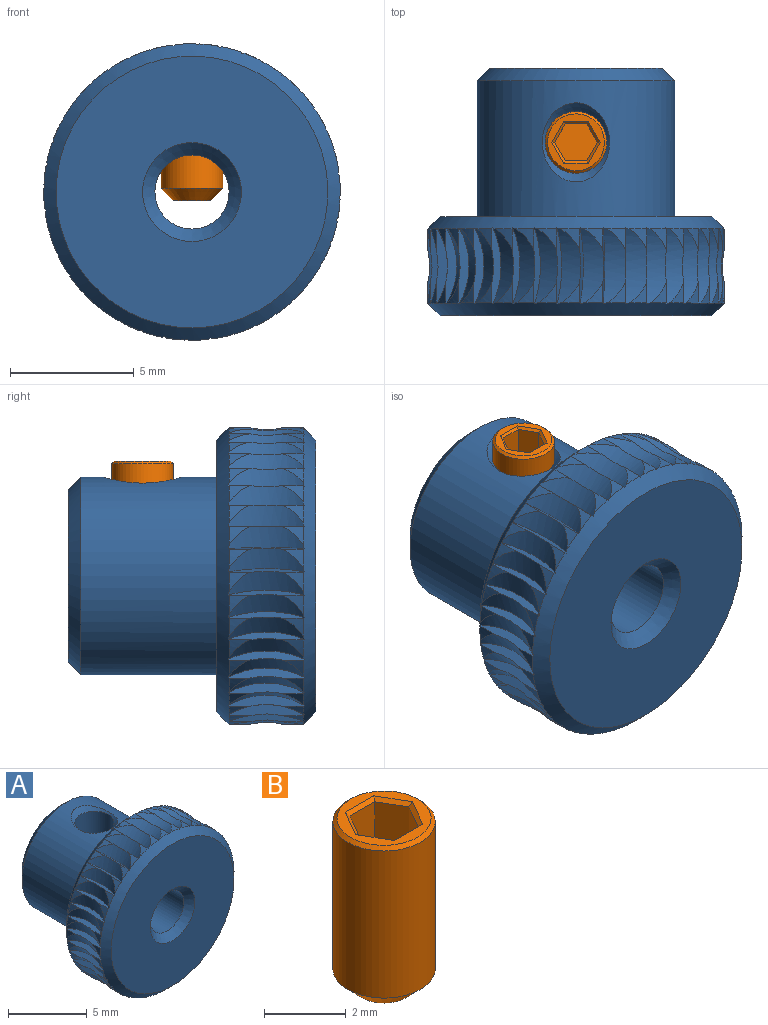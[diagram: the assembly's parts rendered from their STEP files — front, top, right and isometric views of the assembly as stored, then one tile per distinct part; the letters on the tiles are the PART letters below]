
ASSEMBLY  parts=2 mates=1
PART A: 172 faces, bbox 12.6x10x12.6 mm
  f0: cylinder r=1.5mm len=9mm, axis (0,-1,0), area 79.3mm2, adj f167,f168,f170
  f1: cylinder r=4mm len=8mm, axis (0,1,0), area 131.3mm2, adj f164,f165,f171
  f2: cylinder r=6mm len=0.84mm, axis (0,-1,0), area 0.3mm2, adj f129,f130,f169
  f3: cylinder r=6mm len=0.84mm, axis (0,-1,0), area 0.3mm2, adj f127,f128,f169
  f4: cylinder r=6mm len=0.84mm, axis (0,-1,0), area 0.3mm2, adj f125,f126,f169
  f5: cylinder r=6mm len=0.84mm, axis (0,-1,0), area 0.3mm2, adj f119,f124,f169
  f6: cylinder r=6mm len=0.84mm, axis (0,-1,0), area 0.3mm2, adj f122,f123,f169
  f7: cylinder r=6mm len=0.84mm, axis (0,-1,0), area 0.3mm2, adj f120,f121,f169
  f8: cylinder r=6mm len=0.84mm, axis (0,-1,0), area 0.3mm2, adj f116,f117,f169
  f9: cylinder r=6mm len=0.84mm, axis (0,-1,0), area 0.3mm2, adj f86,f115,f169
  f10: cylinder r=6mm len=0.84mm, axis (0,-1,0), area 0.3mm2, adj f113,f114,f169
  f11: cylinder r=6mm len=0.84mm, axis (0,-1,0), area 0.3mm2, adj f111,f112,f169
  f12: cylinder r=6mm len=0.84mm, axis (0,-1,0), area 0.3mm2, adj f109,f110,f169
  f13: cylinder r=6mm len=0.84mm, axis (0,-1,0), area 0.3mm2, adj f103,f108,f169
  f14: cylinder r=6mm len=0.84mm, axis (0,-1,0), area 0.3mm2, adj f106,f107,f169
  f15: cylinder r=6mm len=0.84mm, axis (0,-1,0), area 0.3mm2, adj f104,f105,f169
  f16: cylinder r=6mm len=0.84mm, axis (0,-1,0), area 0.3mm2, adj f101,f102,f169
  f17: cylinder r=6mm len=0.84mm, axis (0,-1,0), area 0.3mm2, adj f87,f100,f169
  f18: cylinder r=6mm len=0.84mm, axis (0,-1,0), area 0.3mm2, adj f98,f99,f169
  f19: cylinder r=6mm len=0.84mm, axis (0,-1,0), area 0.3mm2, adj f96,f97,f169
  f20: cylinder r=6mm len=0.84mm, axis (0,-1,0), area 0.3mm2, adj f94,f95,f169
  f21: cylinder r=6mm len=0.84mm, axis (0,-1,0), area 0.3mm2, adj f88,f93,f169
  f22: cylinder r=6mm len=0.84mm, axis (0,-1,0), area 0.3mm2, adj f91,f92,f169
  f23: cylinder r=6mm len=0.84mm, axis (0,-1,0), area 0.3mm2, adj f89,f90,f169
  f24: cylinder r=6mm len=0.84mm, axis (0,-1,0), area 0.3mm2, adj f84,f162,f169
  f25: cylinder r=6mm len=0.84mm, axis (0,-1,0), area 0.3mm2, adj f160,f161,f169
  f26: cylinder r=6mm len=0.84mm, axis (0,-1,0), area 0.3mm2, adj f83,f159,f169
  f27: cylinder r=6mm len=0.84mm, axis (0,-1,0), area 0.3mm2, adj f157,f158,f169
  f28: cylinder r=6mm len=0.84mm, axis (0,-1,0), area 0.3mm2, adj f155,f156,f169
  f29: cylinder r=6mm len=0.84mm, axis (0,-1,0), area 0.3mm2, adj f149,f154,f169
  f30: cylinder r=6mm len=0.84mm, axis (0,-1,0), area 0.3mm2, adj f152,f153,f169
  f31: cylinder r=6mm len=0.84mm, axis (0,-1,0), area 0.3mm2, adj f150,f151,f169
  f32: cylinder r=6mm len=0.84mm, axis (0,-1,0), area 0.3mm2, adj f147,f148,f169
  f33: cylinder r=6mm len=0.84mm, axis (0,-1,0), area 0.3mm2, adj f85,f146,f169
  f34: cylinder r=6mm len=0.84mm, axis (0,-1,0), area 0.3mm2, adj f144,f145,f169
  f35: cylinder r=6mm len=0.84mm, axis (0,-1,0), area 0.3mm2, adj f142,f143,f169
  f36: cylinder r=6mm len=0.84mm, axis (0,-1,0), area 0.3mm2, adj f140,f141,f169
  f37: cylinder r=6mm len=0.84mm, axis (0,-1,0), area 0.3mm2, adj f134,f139,f169
  f38: cylinder r=6mm len=0.84mm, axis (0,-1,0), area 0.3mm2, adj f137,f138,f169
  f39: cylinder r=6mm len=0.84mm, axis (0,-1,0), area 0.3mm2, adj f135,f136,f169
  f40: cylinder r=6mm len=0.84mm, axis (0,-1,0), area 0.3mm2, adj f132,f133,f169
  f41: cylinder r=6mm len=0.84mm, axis (0,-1,0), area 0.3mm2, adj f122,f123,f166
  f42: cylinder r=6mm len=0.84mm, axis (0,-1,0), area 0.3mm2, adj f119,f124,f166
  f43: cylinder r=6mm len=0.84mm, axis (0,-1,0), area 0.3mm2, adj f125,f126,f166
  f44: cylinder r=6mm len=0.84mm, axis (0,-1,0), area 0.3mm2, adj f127,f128,f166
  f45: cylinder r=6mm len=0.84mm, axis (0,-1,0), area 0.3mm2, adj f129,f130,f166
  f46: cylinder r=6mm len=0.84mm, axis (0,-1,0), area 0.3mm2, adj f118,f131,f166
  f47: cylinder r=6mm len=0.84mm, axis (0,-1,0), area 0.3mm2, adj f132,f133,f166
  f48: cylinder r=6mm len=0.84mm, axis (0,-1,0), area 0.3mm2, adj f135,f136,f166
  f49: cylinder r=6mm len=0.84mm, axis (0,-1,0), area 0.3mm2, adj f137,f138,f166
  f50: cylinder r=6mm len=0.84mm, axis (0,-1,0), area 0.3mm2, adj f134,f139,f166
  f51: cylinder r=6mm len=0.84mm, axis (0,-1,0), area 0.3mm2, adj f140,f141,f166
  f52: cylinder r=6mm len=0.84mm, axis (0,-1,0), area 0.3mm2, adj f142,f143,f166
  f53: cylinder r=6mm len=0.84mm, axis (0,-1,0), area 0.3mm2, adj f144,f145,f166
  f54: cylinder r=6mm len=0.84mm, axis (0,-1,0), area 0.3mm2, adj f85,f146,f166
  f55: cylinder r=6mm len=0.84mm, axis (0,-1,0), area 0.3mm2, adj f147,f148,f166
  f56: cylinder r=6mm len=0.84mm, axis (0,-1,0), area 0.3mm2, adj f150,f151,f166
  f57: cylinder r=6mm len=0.84mm, axis (0,-1,0), area 0.3mm2, adj f152,f153,f166
  f58: cylinder r=6mm len=0.84mm, axis (0,-1,0), area 0.3mm2, adj f149,f154,f166
  f59: cylinder r=6mm len=0.84mm, axis (0,-1,0), area 0.3mm2, adj f155,f156,f166
  f60: cylinder r=6mm len=0.84mm, axis (0,-1,0), area 0.3mm2, adj f157,f158,f166
  f61: cylinder r=6mm len=0.84mm, axis (0,-1,0), area 0.3mm2, adj f83,f159,f166
  f62: cylinder r=6mm len=0.84mm, axis (0,-1,0), area 0.3mm2, adj f160,f161,f166
  f63: cylinder r=6mm len=0.84mm, axis (0,-1,0), area 0.3mm2, adj f84,f162,f166
  f64: cylinder r=6mm len=0.84mm, axis (0,-1,0), area 0.3mm2, adj f89,f90,f166
  f65: cylinder r=6mm len=0.84mm, axis (0,-1,0), area 0.3mm2, adj f91,f92,f166
  f66: cylinder r=6mm len=0.84mm, axis (0,-1,0), area 0.3mm2, adj f88,f93,f166
  f67: cylinder r=6mm len=0.84mm, axis (0,-1,0), area 0.3mm2, adj f94,f95,f166
  f68: cylinder r=6mm len=0.84mm, axis (0,-1,0), area 0.3mm2, adj f96,f97,f166
  f69: cylinder r=6mm len=0.84mm, axis (0,-1,0), area 0.3mm2, adj f98,f99,f166
  f70: cylinder r=6mm len=0.84mm, axis (0,-1,0), area 0.3mm2, adj f87,f100,f166
  f71: cylinder r=6mm len=0.84mm, axis (0,-1,0), area 0.3mm2, adj f101,f102,f166
  f72: cylinder r=6mm len=0.84mm, axis (0,-1,0), area 0.3mm2, adj f104,f105,f166
  f73: cylinder r=6mm len=0.84mm, axis (0,-1,0), area 0.3mm2, adj f106,f107,f166
  f74: cylinder r=6mm len=0.84mm, axis (0,-1,0), area 0.3mm2, adj f103,f108,f166
  f75: cylinder r=6mm len=0.84mm, axis (0,-1,0), area 0.3mm2, adj f109,f110,f166
  f76: cylinder r=6mm len=0.84mm, axis (0,-1,0), area 0.3mm2, adj f111,f112,f166
  f77: cylinder r=6mm len=0.84mm, axis (0,-1,0), area 0.3mm2, adj f113,f114,f166
  f78: cylinder r=6mm len=0.84mm, axis (0,-1,0), area 0.3mm2, adj f86,f115,f166
  f79: cylinder r=6mm len=0.84mm, axis (0,-1,0), area 0.3mm2, adj f116,f117,f166
  f80: cylinder r=6mm len=0.84mm, axis (0,-1,0), area 0.3mm2, adj f120,f121,f166
  f81: cylinder r=6mm len=0.84mm, axis (0,-1,0), area 0.3mm2, adj f118,f131,f169
  f82: plane 11x11mm, normal (0,-1,0), area 82.5mm2, adj f168,f169
  f83: cylinder r=3mm len=3.07mm, axis (-0.16,0,-0.99), area 2.2mm2, adj f26,f61,f159,f160,f166,f169
  f84: cylinder r=3mm len=3.07mm, axis (0.16,0,-0.99), area 2.2mm2, adj f24,f63,f90,f162,f166,f169
  f85: cylinder r=3mm len=3.07mm, axis (-0.95,0,-0.31), area 2.2mm2, adj f33,f54,f146,f147,f166,f169
  f86: cylinder r=3mm len=3.07mm, axis (0.59,0,0.81), area 2.2mm2, adj f9,f78,f115,f116,f166,f169
  f87: cylinder r=3mm len=3.07mm, axis (0.95,0,-0.31), area 2.2mm2, adj f17,f70,f100,f101,f166,f169
  f88: cylinder r=3mm len=3.07mm, axis (0.59,0,-0.81), area 2.2mm2, adj f21,f66,f93,f94,f166,f169
  f89: cylinder r=3mm len=3.07mm, axis (0.31,0,-0.95), area 2.2mm2, adj f23,f64,f90,f91,f166,f169
  f90: plane 3.09x0.47mm, normal (-0.16,0,0.99), area 0.9mm2, adj f23,f64,f84,f89,f166,f169
  f91: plane 3.09x0.46mm, normal (-0.31,0,0.95), area 0.9mm2, adj f22,f65,f89,f92,f166,f169
  f92: cylinder r=3mm len=3.07mm, axis (0.45,0,-0.89), area 2.2mm2, adj f22,f65,f91,f93,f166,f169
  f93: plane 3.09x0.43mm, normal (-0.45,0,0.89), area 0.9mm2, adj f21,f66,f88,f92,f166,f169
  f94: plane 3.09x0.39mm, normal (-0.59,0,0.81), area 0.9mm2, adj f20,f67,f88,f95,f166,f169
  f95: cylinder r=3mm len=3.07mm, axis (0.71,0,-0.71), area 2.2mm2, adj f20,f67,f94,f97,f166,f169
  f96: cylinder r=3mm len=3.07mm, axis (0.81,0,-0.59), area 2.2mm2, adj f19,f68,f97,f98,f166,f169
  f97: plane 3.09x0.35mm, normal (-0.71,0,0.71), area 0.9mm2, adj f19,f68,f95,f96,f166,f169
  f98: plane 3.09x0.39mm, normal (-0.81,0,0.59), area 0.9mm2, adj f18,f69,f96,f99,f166,f169
  f99: cylinder r=3mm len=3.07mm, axis (0.89,0,-0.45), area 2.2mm2, adj f18,f69,f98,f100,f166,f169
  f100: plane 3.09x0.43mm, normal (-0.89,0,0.45), area 0.9mm2, adj f17,f70,f87,f99,f166,f169
  f101: plane 3.09x0.46mm, normal (-0.95,0,0.31), area 0.9mm2, adj f16,f71,f87,f102,f166,f169
  f102: cylinder r=3mm len=3.07mm, axis (0.99,0,-0.16), area 2.2mm2, adj f16,f71,f101,f105,f166,f169
  f103: cylinder r=3mm len=3.07mm, axis (0.95,0,0.31), area 2.2mm2, adj f13,f74,f108,f109,f166,f169
  f104: cylinder r=3mm len=3.07mm, axis (1,0,0), area 2.2mm2, adj f15,f72,f105,f106,f166,f169
  f105: plane 3.09x0.47mm, normal (-0.99,0,0.16), area 0.9mm2, adj f15,f72,f102,f104,f166,f169
  f106: plane 3.09x0.48mm, normal (-1,0,0), area 0.9mm2, adj f14,f73,f104,f107,f166,f169
  f107: cylinder r=3mm len=3.07mm, axis (0.99,0,0.16), area 2.2mm2, adj f14,f73,f106,f108,f166,f169
  f108: plane 3.09x0.47mm, normal (-0.99,0,-0.16), area 0.9mm2, adj f13,f74,f103,f107,f166,f169
  f109: plane 3.09x0.46mm, normal (-0.95,0,-0.31), area 0.9mm2, adj f12,f75,f103,f110,f166,f169
  f110: cylinder r=3mm len=3.07mm, axis (0.89,0,0.45), area 2.2mm2, adj f12,f75,f109,f112,f166,f169
  f111: cylinder r=3mm len=3.07mm, axis (0.81,0,0.59), area 2.2mm2, adj f11,f76,f112,f113,f166,f169
  f112: plane 3.09x0.43mm, normal (-0.89,0,-0.45), area 0.9mm2, adj f11,f76,f110,f111,f166,f169
  f113: plane 3.09x0.39mm, normal (-0.81,0,-0.59), area 0.9mm2, adj f10,f77,f111,f114,f166,f169
  f114: cylinder r=3mm len=3.07mm, axis (0.71,0,0.71), area 2.2mm2, adj f10,f77,f113,f115,f166,f169
  f115: plane 3.09x0.35mm, normal (-0.71,0,-0.71), area 0.9mm2, adj f9,f78,f86,f114,f166,f169
  f116: plane 3.09x0.39mm, normal (-0.59,0,-0.81), area 0.9mm2, adj f8,f79,f86,f117,f166,f169
  f117: cylinder r=3mm len=3.07mm, axis (0.45,0,0.89), area 2.2mm2, adj f8,f79,f116,f121,f166,f169
  f118: cylinder r=3mm len=3.07mm, axis (-0.59,0,0.81), area 2.2mm2, adj f46,f81,f131,f132,f166,f169
  f119: cylinder r=3mm len=3.07mm, axis (0,0,1), area 2.2mm2, adj f5,f42,f124,f125,f166,f169
  f120: cylinder r=3mm len=3.07mm, axis (0.31,0,0.95), area 2.2mm2, adj f7,f80,f121,f122,f166,f169
  f121: plane 3.09x0.43mm, normal (-0.45,0,-0.89), area 0.9mm2, adj f7,f80,f117,f120,f166,f169
  f122: plane 3.09x0.46mm, normal (-0.31,0,-0.95), area 0.9mm2, adj f6,f41,f120,f123,f166,f169
  f123: cylinder r=3mm len=3.07mm, axis (0.16,0,0.99), area 2.2mm2, adj f6,f41,f122,f124,f166,f169
  f124: plane 3.09x0.47mm, normal (-0.16,0,-0.99), area 0.9mm2, adj f5,f42,f119,f123,f166,f169
  f125: plane 3.09x0.48mm, normal (0,0,-1), area 0.9mm2, adj f4,f43,f119,f126,f166,f169
  f126: cylinder r=3mm len=3.07mm, axis (-0.16,0,0.99), area 2.2mm2, adj f4,f43,f125,f128,f166,f169
  f127: cylinder r=3mm len=3.07mm, axis (-0.31,0,0.95), area 2.2mm2, adj f3,f44,f128,f129,f166,f169
  f128: plane 3.09x0.47mm, normal (0.16,0,-0.99), area 0.9mm2, adj f3,f44,f126,f127,f166,f169
  f129: plane 3.09x0.46mm, normal (0.31,0,-0.95), area 0.9mm2, adj f2,f45,f127,f130,f166,f169
  f130: cylinder r=3mm len=3.07mm, axis (-0.45,0,0.89), area 2.2mm2, adj f2,f45,f129,f131,f166,f169
  f131: plane 3.09x0.43mm, normal (0.45,0,-0.89), area 0.9mm2, adj f46,f81,f118,f130,f166,f169
  f132: plane 3.09x0.39mm, normal (0.59,0,-0.81), area 0.9mm2, adj f40,f47,f118,f133,f166,f169
  f133: cylinder r=3mm len=3.07mm, axis (-0.71,0,0.71), area 2.2mm2, adj f40,f47,f132,f136,f166,f169
  f134: cylinder r=3mm len=3.07mm, axis (-0.95,0,0.31), area 2.2mm2, adj f37,f50,f139,f140,f166,f169
  f135: cylinder r=3mm len=3.07mm, axis (-0.81,0,0.59), area 2.2mm2, adj f39,f48,f136,f137,f166,f169
  f136: plane 3.09x0.35mm, normal (0.71,0,-0.71), area 0.9mm2, adj f39,f48,f133,f135,f166,f169
  f137: plane 3.09x0.39mm, normal (0.81,0,-0.59), area 0.9mm2, adj f38,f49,f135,f138,f166,f169
  f138: cylinder r=3mm len=3.07mm, axis (-0.89,0,0.45), area 2.2mm2, adj f38,f49,f137,f139,f166,f169
  f139: plane 3.09x0.43mm, normal (0.89,0,-0.45), area 0.9mm2, adj f37,f50,f134,f138,f166,f169
  f140: plane 3.09x0.46mm, normal (0.95,0,-0.31), area 0.9mm2, adj f36,f51,f134,f141,f166,f169
  f141: cylinder r=3mm len=3.07mm, axis (-0.99,0,0.16), area 2.2mm2, adj f36,f51,f140,f143,f166,f169
  f142: cylinder r=3mm len=3.07mm, axis (-1,0,0), area 2.2mm2, adj f35,f52,f143,f144,f166,f169
  f143: plane 3.09x0.47mm, normal (0.99,0,-0.16), area 0.9mm2, adj f35,f52,f141,f142,f166,f169
  f144: plane 3.09x0.48mm, normal (1,0,0), area 0.9mm2, adj f34,f53,f142,f145,f166,f169
  f145: cylinder r=3mm len=3.07mm, axis (-0.99,0,-0.16), area 2.2mm2, adj f34,f53,f144,f146,f166,f169
  f146: plane 3.09x0.47mm, normal (0.99,0,0.16), area 0.9mm2, adj f33,f54,f85,f145,f166,f169
  f147: plane 3.09x0.46mm, normal (0.95,0,0.31), area 0.9mm2, adj f32,f55,f85,f148,f166,f169
  f148: cylinder r=3mm len=3.07mm, axis (-0.89,0,-0.45), area 2.2mm2, adj f32,f55,f147,f151,f166,f169
  f149: cylinder r=3mm len=3.07mm, axis (-0.59,0,-0.81), area 2.2mm2, adj f29,f58,f154,f155,f166,f169
  f150: cylinder r=3mm len=3.07mm, axis (-0.81,0,-0.59), area 2.2mm2, adj f31,f56,f151,f152,f166,f169
  f151: plane 3.09x0.43mm, normal (0.89,0,0.45), area 0.9mm2, adj f31,f56,f148,f150,f166,f169
  f152: plane 3.09x0.39mm, normal (0.81,0,0.59), area 0.9mm2, adj f30,f57,f150,f153,f166,f169
  f153: cylinder r=3mm len=3.07mm, axis (-0.71,0,-0.71), area 2.2mm2, adj f30,f57,f152,f154,f166,f169
  f154: plane 3.09x0.35mm, normal (0.71,0,0.71), area 0.9mm2, adj f29,f58,f149,f153,f166,f169
  f155: plane 3.09x0.39mm, normal (0.59,0,0.81), area 0.9mm2, adj f28,f59,f149,f156,f166,f169
  f156: cylinder r=3mm len=3.07mm, axis (-0.45,0,-0.89), area 2.2mm2, adj f28,f59,f155,f158,f166,f169
  f157: cylinder r=3mm len=3.07mm, axis (-0.31,0,-0.95), area 2.2mm2, adj f27,f60,f158,f159,f166,f169
  f158: plane 3.09x0.43mm, normal (0.45,0,0.89), area 0.9mm2, adj f27,f60,f156,f157,f166,f169
  f159: plane 3.09x0.46mm, normal (0.31,0,0.95), area 0.9mm2, adj f26,f61,f83,f157,f166,f169
  f160: plane 3.09x0.47mm, normal (0.16,0,0.99), area 0.9mm2, adj f25,f62,f83,f161,f166,f169
  f161: cylinder r=3mm len=3.07mm, axis (0,0,-1), area 2.2mm2, adj f25,f62,f160,f162,f166,f169
  f162: plane 3.09x0.48mm, normal (0,0,1), area 0.9mm2, adj f24,f63,f84,f161,f166,f169
  f163: plane 7x7mm, normal (0,1,0), area 25.9mm2, adj f165,f167
  f164: plane 11x11mm, normal (0,1,0), area 44.8mm2, adj f1,f166
  f165: cone r=3.5mm half-angle=45deg, axis (0,-1,0), area 16.7mm2, adj f1,f163
  f166: cone r=6mm half-angle=45deg, axis (0,-1,0), area 25.4mm2, adj f41,f42,f43,f44,f45,f46,f47,f48
  f167: cone r=1.5mm half-angle=45deg, axis (0,1,0), area 7.8mm2, adj f0,f163
  f168: cone r=1.5mm half-angle=45deg, axis (0,-1,0), area 7.8mm2, adj f0,f82
  f169: cone r=5.5mm half-angle=45deg, axis (0,1,0), area 25.4mm2, adj f2,f3,f4,f5,f6,f7,f8,f9
  f170: cylinder r=1.25mm len=2.82mm, axis (0,0,1), area 19.3mm2, adj f0,f171
  f171: cone r=1.25mm half-angle=45deg, axis (0,0,1), area 2.7mm2, adj f1,f170
PART B: 18 faces, bbox 2.5x2.5x5 mm
  f0: plane 2.3x2.3mm, normal (0,0,1), area 1.7mm2, adj f10,f11,f12,f13,f14,f15,f16
  f1: cylinder r=1.25mm len=4.4mm, axis (0,0,1), area 34.6mm2, adj f16,f17
  f2: plane 1.5x1.5mm, normal (0,0,-1), area 1.8mm2, adj f17
  f3: plane 1.4x0.75mm, normal (0.87,-0.5,0), area 1.2mm2, adj f4,f8,f9,f15
  f4: plane 1.4x0.75mm, normal (0.87,0.5,0), area 1.2mm2, adj f3,f5,f9,f13
  f5: plane 1.4x0.87mm, normal (0,1,0), area 1.2mm2, adj f4,f6,f9,f11
  f6: plane 1.4x0.75mm, normal (-0.87,0.5,0), area 1.2mm2, adj f5,f7,f9,f10
  f7: plane 1.4x0.75mm, normal (-0.87,-0.5,0), area 1.2mm2, adj f6,f8,f9,f12
  f8: plane 1.4x0.87mm, normal (0,-1,0), area 1.2mm2, adj f3,f7,f9,f14
  f9: plane 1.73x1.5mm, normal (0,0,1), area 1.9mm2, adj f3,f4,f5,f6,f7,f8
  f10: plane 0.85x0.55mm, normal (-0.61,0.35,0.71), area 0.1mm2, adj f0,f6,f11,f12
  f11: plane 0.98x0.1mm, normal (0,0.71,0.71), area 0.1mm2, adj f0,f5,f10,f13
  f12: plane 0.85x0.55mm, normal (-0.61,-0.35,0.71), area 0.1mm2, adj f0,f7,f10,f14
  f13: plane 0.85x0.55mm, normal (0.61,0.35,0.71), area 0.1mm2, adj f0,f4,f11,f15
  f14: plane 0.98x0.1mm, normal (0,-0.71,0.71), area 0.1mm2, adj f0,f8,f12,f15
  f15: plane 0.85x0.55mm, normal (0.61,-0.35,0.71), area 0.1mm2, adj f0,f3,f13,f14
  f16: cone r=1.15mm half-angle=45deg, axis (0,0,-1), area 1.1mm2, adj f0,f1
  f17: cone r=1.25mm half-angle=45deg, axis (0,0,1), area 4.4mm2, adj f1,f2
PLACE A t=(-0.93,-5.71,1.74)mm
PLACE B t=(-0.93,1.29,4.39)mm
MATE fastened B.f1 <-> A.f170  axis (0,0,1) through (-0.93,1.29,4.39)mm
